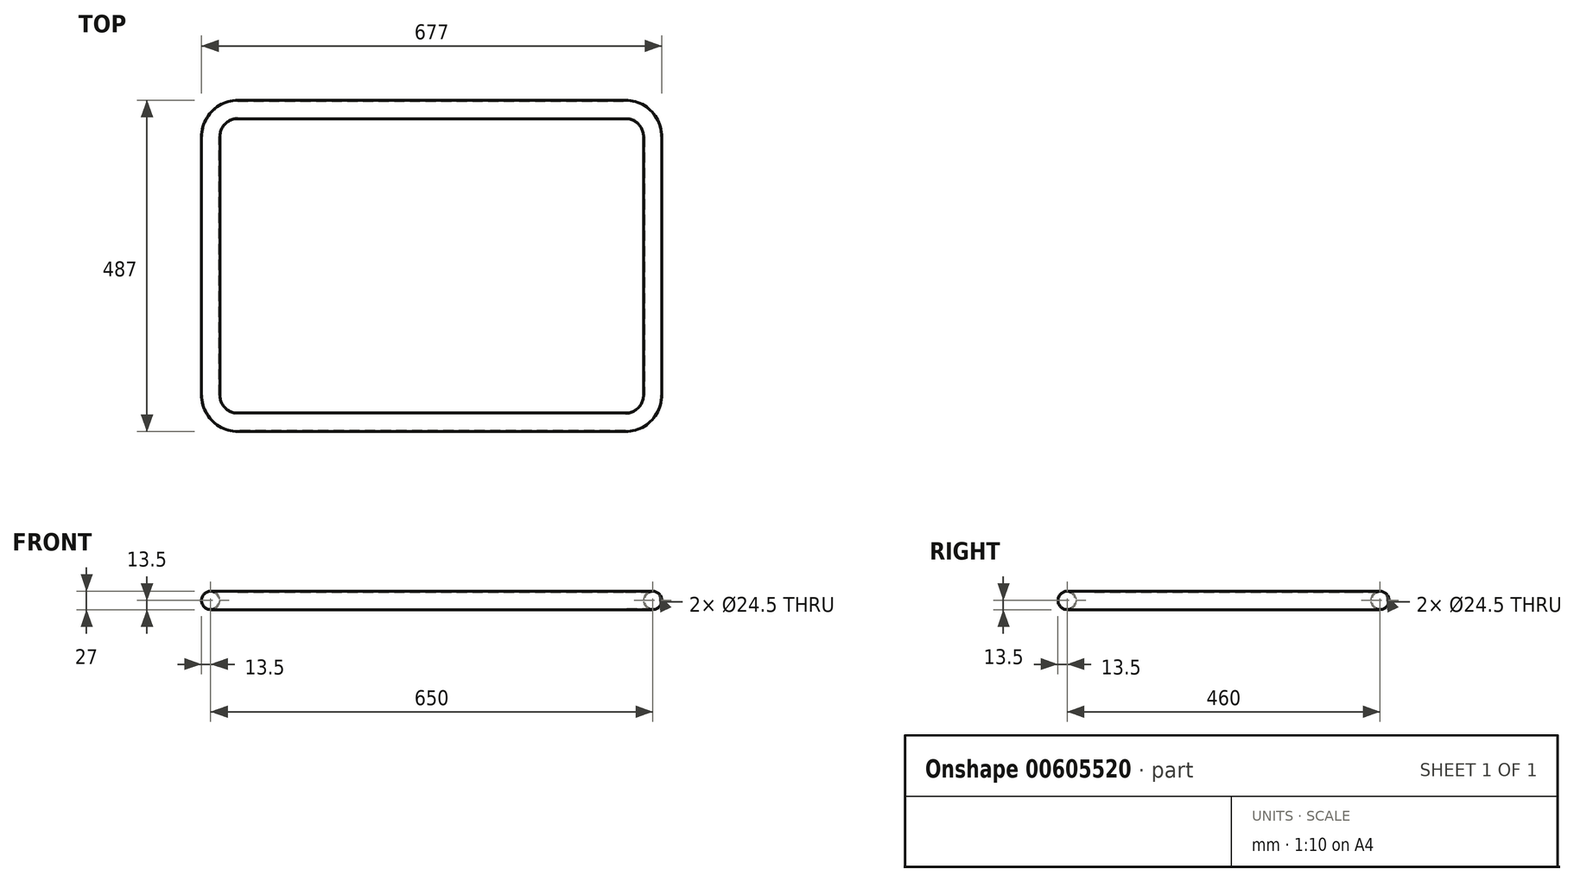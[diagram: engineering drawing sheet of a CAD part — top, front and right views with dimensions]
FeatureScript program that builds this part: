
annotation { "Feature Type Name" : "Feature", "Feature Type Description" : "" }
export const myFeature = defineFeature(function(context is Context, id is Id, definition is map)
    precondition{}
    {
        {
            var Q0;
            Q0=qCreatedBy(makeId("Right.planeOp"),FACE);
            var sketch = newSketch(context, id + "F0", { "sketchPlane" : qUnion([Q0])});
            skCircle(sketch, "E0", {"center": v(0, 0) * mm, "radius": 12.25 * mm});
            skCircle(sketch, "E1", {"center": v(0, 0) * mm, "radius": 13.5 * mm});
            skSolve(sketch);
        }
        {
            var Q0;
            Q0=qCreatedBy(makeId("Top.planeOp"),FACE);
            var sketch = newSketch(context, id + "F1", { "sketchPlane" : qUnion([Q0])});
            skLineSegment(sketch, "E2", {"start": v(0, 0) * mm, "end": v(285, 0) * mm});
            skLineSegment(sketch, "E3", {"start": v(325, -40) * mm, "end": v(325, -420) * mm});
            skLineSegment(sketch, "E4", {"start": v(285, -460) * mm, "end": v(-285, -460) * mm});
            skLineSegment(sketch, "E5", {"start": v(-325, -420) * mm, "end": v(-325, -40) * mm});
            skLineSegment(sketch, "E6", {"start": v(-285, 0) * mm, "end": v(0, 0) * mm});
            skPoint(sketch, "E7.visualSharp", {"position": v(325, 0) * mm});
            skArc(sketch, "E7.filletArc", {"start": v(325, -40) * mm, "mid": v(313.28, -11.72) * mm, "end": v(285, 0) * mm});
            skPoint(sketch, "E8.visualSharp", {"position": v(325, -460) * mm});
            skArc(sketch, "E8.filletArc", {"start": v(285, -460) * mm, "mid": v(313.28, -448.28) * mm, "end": v(325, -420) * mm});
            skPoint(sketch, "E9.visualSharp", {"position": v(-325, -460) * mm});
            skArc(sketch, "E9.filletArc", {"start": v(-325, -420) * mm, "mid": v(-313.28, -448.28) * mm, "end": v(-285, -460) * mm});
            skPoint(sketch, "E10.visualSharp", {"position": v(-325, 0) * mm});
            skArc(sketch, "E10.filletArc", {"start": v(-285, 0) * mm, "mid": v(-313.28, -11.72) * mm, "end": v(-325, -40) * mm});
            skSolve(sketch);
        }
        {
            var Q0;
            Q0=makeQuery(id+"F0.imprint","IMPRINT",FACE,{"disambiguationData":[TD([[makeQuery(id+"F0.imprint","IMPRINT",EDGE,{"derivedFrom":sQuery(id+"F0.wireOp",EDGE,"E0")}),-1.0]])]});
            var Q1;
            Q1=sQuery(id+"F1.wireOp",EDGE,"E2");
            var Q2;
            Q2=sQuery(id+"F1.wireOp",EDGE,"E7.filletArc");
            var Q3;
            Q3=sQuery(id+"F1.wireOp",EDGE,"E3");
            var Q4;
            Q4=sQuery(id+"F1.wireOp",EDGE,"E8.filletArc");
            var Q5;
            Q5=sQuery(id+"F1.wireOp",EDGE,"E4");
            var Q6;
            Q6=sQuery(id+"F1.wireOp",EDGE,"E9.filletArc");
            var Q7;
            Q7=sQuery(id+"F1.wireOp",EDGE,"E5");
            var Q8;
            Q8=sQuery(id+"F1.wireOp",EDGE,"E10.filletArc");
            var Q9;
            Q9=sQuery(id+"F1.wireOp",EDGE,"E6");
            sweep(context, id + "F2", {"profiles" : qUnion([Q0]), "path" : qUnion([Q1, Q2, Q3, Q4, Q5, Q6, Q7, Q8, Q9])});
        }
    });
